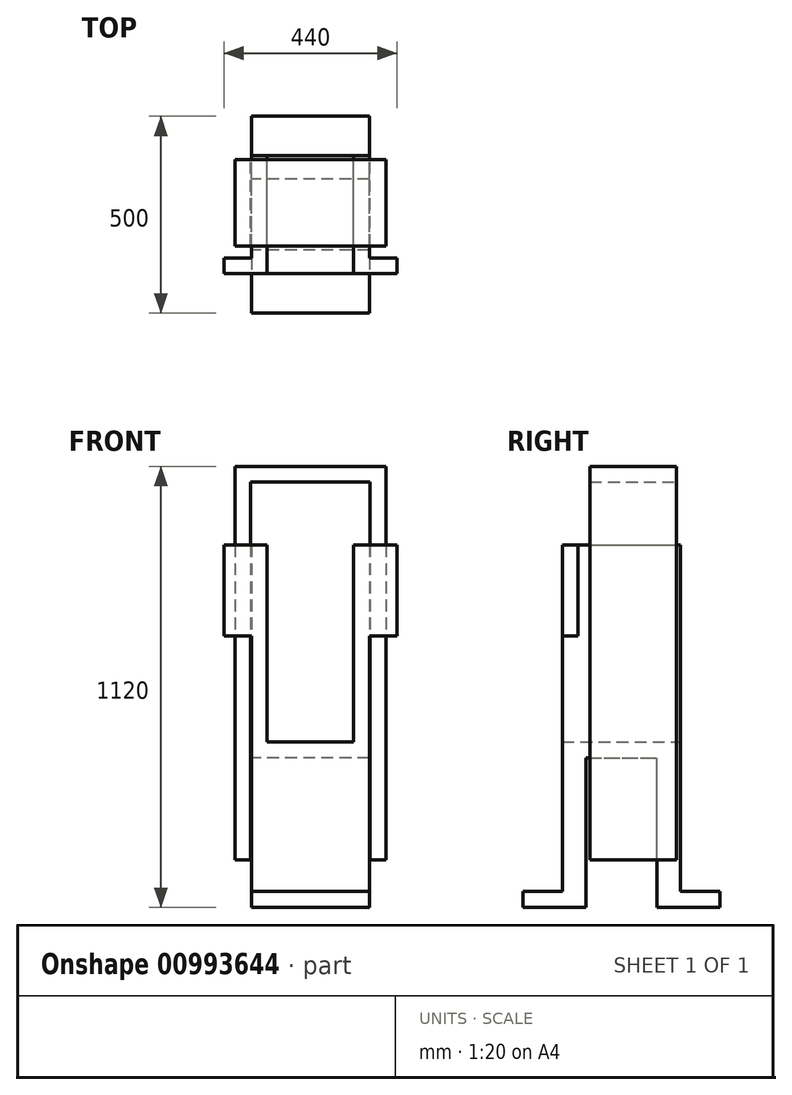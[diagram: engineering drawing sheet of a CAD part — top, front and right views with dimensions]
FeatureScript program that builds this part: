
annotation { "Feature Type Name" : "Feature", "Feature Type Description" : "" }
export const myFeature = defineFeature(function(context is Context, id is Id, definition is map)
    precondition{}
    {
        {
            var Q0;
            Q0=qCreatedBy(makeId("Top.planeOp"),FACE);
            var sketch = newSketch(context, id + "F0", { "sketchPlane" : qUnion([Q0])});
            skLineSegment(sketch, "E0.bottom", {"start": v(150, -150) * mm, "end": v(-150, -150) * mm});
            skLineSegment(sketch, "E0.top", {"start": v(150, 150) * mm, "end": v(-150, 150) * mm});
            skLineSegment(sketch, "E0.left", {"start": v(150, -150) * mm, "end": v(150, 150) * mm});
            skLineSegment(sketch, "E0.right", {"start": v(-150, -150) * mm, "end": v(-150, 150) * mm});
            skPoint(sketch, "E0.middle", {"position": v(0, 0) * mm});
            skSolve(sketch);
        }
        {
            var Q0;
            Q0=makeQuery(id+"F0.imprint","IMPRINT",FACE,{"disambiguationData":[TD([[makeQuery(id+"F0.imprint","IMPRINT",EDGE,{"derivedFrom":sQuery(id+"F0.wireOp",EDGE,"E0.bottom")}),-1.0]])]});
            extrude(context, id + "F1", {"entities" : qUnion([Q0]), "depth" : 40 * mm, "offsetDistance" : 25 * mm});
        }
        {
            var Q0;
            Q0=makeQuery(id+"F1.opExtrude","CAP_FACE",FACE,{"disambiguationData":[OSD([sQuery(id+"F0.wireOp",EDGE,"E0.bottom"),sQuery(id+"F0.wireOp",EDGE,"E0.top"),sQuery(id+"F0.wireOp",EDGE,"E0.left"),sQuery(id+"F0.wireOp",EDGE,"E0.right")])],"isStart":false});
            var sketch = newSketch(context, id + "F2", { "sketchPlane" : qUnion([Q0])});
            skLineSegment(sketch, "E1.bottom", {"start": v(-150, -150) * mm, "end": v(-110, -150) * mm});
            skLineSegment(sketch, "E1.top", {"start": v(-150, 150) * mm, "end": v(-110, 150) * mm});
            skLineSegment(sketch, "E1.left", {"start": v(-150, -150) * mm, "end": v(-150, 150) * mm});
            skLineSegment(sketch, "E1.right", {"start": v(-110, -150) * mm, "end": v(-110, 150) * mm});
            skLineSegment(sketch, "E2.bottom", {"start": v(150, -150) * mm, "end": v(110, -150) * mm});
            skLineSegment(sketch, "E2.top", {"start": v(150, 150) * mm, "end": v(110, 150) * mm});
            skLineSegment(sketch, "E2.left", {"start": v(150, -150) * mm, "end": v(150, 150) * mm});
            skLineSegment(sketch, "E2.right", {"start": v(110, -150) * mm, "end": v(110, 150) * mm});
            skSolve(sketch);
        }
        {
            var Q0;
            Q0=makeQuery(id+"F2.imprint","IMPRINT",FACE,{"disambiguationData":[TD([[makeQuery(id+"F2.imprint","IMPRINT",EDGE,{"derivedFrom":sQuery(id+"F2.wireOp",EDGE,"E1.bottom")}),-1.0]])]});
            var Q1;
            Q1=makeQuery(id+"F2.imprint","IMPRINT",FACE,{"disambiguationData":[TD([[makeQuery(id+"F2.imprint","IMPRINT",EDGE,{"derivedFrom":sQuery(id+"F2.wireOp",EDGE,"E2.bottom")}),-1.0]])]});
            extrude(context, id + "F3", {"entities" : qUnion([Q0, Q1]), "operationType" : NewBodyOperationType.ADD, "depth" : 500 * mm, "offsetDistance" : 25 * mm});
        }
        {
            var Q0;
            Q0=makeQuery(id+"F3.boolean.opBoolean","MERGE",FACE,{"derivedFrom":[makeQuery(id+"F1.opExtrude","SWEPT_FACE",FACE,{"disambiguationData":[OSD([sQuery(id+"F0.wireOp",EDGE,"E0.bottom")])]}),makeQuery(id+"F3.opExtrude","SWEPT_FACE",FACE,{"disambiguationData":[OSD([sQuery(id+"F2.wireOp",EDGE,"E1.bottom")])]}),makeQuery(id+"F3.opExtrude","SWEPT_FACE",FACE,{"disambiguationData":[OSD([sQuery(id+"F2.wireOp",EDGE,"E2.bottom")])]})]});
            var sketch = newSketch(context, id + "F4", { "sketchPlane" : qUnion([Q0])});
            skLineSegment(sketch, "E3.bottom", {"start": v(-150, 540) * mm, "end": v(-220, 540) * mm});
            skLineSegment(sketch, "E3.top", {"start": v(-150, 310) * mm, "end": v(-220, 310) * mm});
            skLineSegment(sketch, "E3.left", {"start": v(-150, 540) * mm, "end": v(-150, 310) * mm});
            skLineSegment(sketch, "E3.right", {"start": v(-220, 540) * mm, "end": v(-220, 310) * mm});
            skLineSegment(sketch, "E4.bottom", {"start": v(150, 540) * mm, "end": v(220, 540) * mm});
            skLineSegment(sketch, "E4.top", {"start": v(150, 310) * mm, "end": v(220, 310) * mm});
            skLineSegment(sketch, "E4.left", {"start": v(150, 540) * mm, "end": v(150, 310) * mm});
            skLineSegment(sketch, "E4.right", {"start": v(220, 540) * mm, "end": v(220, 310) * mm});
            skSolve(sketch);
        }
        {
            var Q0;
            Q0=makeQuery(id+"F4.imprint","IMPRINT",FACE,{"disambiguationData":[TD([[makeQuery(id+"F4.imprint","IMPRINT",EDGE,{"derivedFrom":sQuery(id+"F4.wireOp",EDGE,"E3.bottom")}),1.0]])]});
            var Q1;
            Q1=makeQuery(id+"F4.imprint","IMPRINT",FACE,{"disambiguationData":[TD([[makeQuery(id+"F4.imprint","IMPRINT",EDGE,{"derivedFrom":sQuery(id+"F4.wireOp",EDGE,"E4.bottom")}),-1.0]])]});
            extrude(context, id + "F5", {"entities" : qUnion([Q0, Q1]), "operationType" : NewBodyOperationType.ADD, "oppositeDirection" : true, "depth" : 40 * mm, "offsetDistance" : 25 * mm});
        }
        {
            var Q0;
            Q0=makeQuery(id+"F5.boolean.opBoolean","MERGE",FACE,{"derivedFrom":[makeQuery(id+"F3.opExtrude","CAP_FACE",FACE,{"disambiguationData":[OSD([sQuery(id+"F2.wireOp",EDGE,"E1.bottom"),sQuery(id+"F2.wireOp",EDGE,"E1.top"),sQuery(id+"F2.wireOp",EDGE,"E1.left"),sQuery(id+"F2.wireOp",EDGE,"E1.right")])],"isStart":false}),makeQuery(id+"F5.opExtrude","SWEPT_FACE",FACE,{"disambiguationData":[OSD([sQuery(id+"F4.wireOp",EDGE,"E3.bottom")])]})]});
            var sketch = newSketch(context, id + "F6", { "sketchPlane" : qUnion([Q0])});
            skLineSegment(sketch, "E5.0", {"start": v(-110, 150) * mm, "end": v(-150, 150) * mm, "construction": true});
            skPoint(sketch, "E6.0", {"position": v(220, -110) * mm});
            skPoint(sketch, "E7.0", {"position": v(-220, -110) * mm});
            skPoint(sketch, "E8.0", {"position": v(150, 150) * mm});
            skPoint(sketch, "E9.0", {"position": v(-150, 150) * mm});
            skLineSegment(sketch, "E10.bottom", {"start": v(192, -80) * mm, "end": v(152, -80) * mm});
            skLineSegment(sketch, "E10.top", {"start": v(192, 140) * mm, "end": v(152, 140) * mm});
            skLineSegment(sketch, "E10.left", {"start": v(192, -80) * mm, "end": v(192, 140) * mm});
            skLineSegment(sketch, "E10.right", {"start": v(152, -80) * mm, "end": v(152, 140) * mm});
            skLineSegment(sketch, "E11.MirrorCS", {"start": v(-152, -80) * mm, "end": v(-152, 140) * mm});
            skLineSegment(sketch, "E12.MirrorCS", {"start": v(-192, -80) * mm, "end": v(-192, 140) * mm});
            skLineSegment(sketch, "E13.MirrorCS", {"start": v(-192, 140) * mm, "end": v(-152, 140) * mm});
            skLineSegment(sketch, "E14.MirrorCS", {"start": v(-192, -80) * mm, "end": v(-152, -80) * mm});
            skSolve(sketch);
        }
        {
            var Q0;
            Q0=makeQuery(id+"F6.imprint","IMPRINT",FACE,{"disambiguationData":[TD([[makeQuery(id+"F6.imprint","IMPRINT",EDGE,{"derivedFrom":sQuery(id+"F6.wireOp",EDGE,"E10.bottom")}),-1.0]])]});
            var Q1;
            Q1=makeQuery(id+"F6.imprint","IMPRINT",FACE,{"disambiguationData":[TD([[makeQuery(id+"F6.imprint","IMPRINT",EDGE,{"derivedFrom":sQuery(id+"F6.wireOp",EDGE,"E11.MirrorCS")}),1.0]])]});
            extrude(context, id + "F7", {"entities" : qUnion([Q0, Q1]), "depth" : 200 * mm, "offsetDistance" : 25 * mm});
        }
        {
            var Q0;
            Q0=makeQuery(id+"F7.opExtrude","CAP_FACE",FACE,{"disambiguationData":[OSD([sQuery(id+"F6.wireOp",EDGE,"E10.bottom"),sQuery(id+"F6.wireOp",EDGE,"E10.top"),sQuery(id+"F6.wireOp",EDGE,"E10.left"),sQuery(id+"F6.wireOp",EDGE,"E10.right")])],"isStart":false});
            var sketch = newSketch(context, id + "F8", { "sketchPlane" : qUnion([Q0])});
            skPoint(sketch, "E15.0", {"position": v(-192, 140) * mm});
            skPoint(sketch, "E16.0", {"position": v(192, -80) * mm});
            skLineSegment(sketch, "E17.bottom", {"start": v(192, -80) * mm, "end": v(-192, -80) * mm});
            skLineSegment(sketch, "E17.top", {"start": v(192, 140) * mm, "end": v(-192, 140) * mm});
            skLineSegment(sketch, "E17.left", {"start": v(192, -80) * mm, "end": v(192, 140) * mm});
            skLineSegment(sketch, "E17.right", {"start": v(-192, -80) * mm, "end": v(-192, 140) * mm});
            skSolve(sketch);
        }
        {
            var Q0;
            {var subQ2=sQuery(id+"F8.wireOp",EDGE,"E17.right");Q0=makeQuery(id+"F8.imprint","IMPRINT",FACE,{"disambiguationData":[TD([[makeQuery(id+"F8.imprint","IMPRINT",EDGE,{"derivedFrom":subQ2}),-1.0]])]});}
            extrude(context, id + "F9", {"entities" : qUnion([Q0]), "operationType" : NewBodyOperationType.ADD, "oppositeDirection" : true, "depth" : 40 * mm, "offsetDistance" : 25 * mm});
        }
        {
            var Q0;
            Q0=makeQuery(id+"F7.opExtrude","CAP_FACE",FACE,{"disambiguationData":[OSD([sQuery(id+"F6.wireOp",EDGE,"E10.bottom"),sQuery(id+"F6.wireOp",EDGE,"E10.top"),sQuery(id+"F6.wireOp",EDGE,"E10.left"),sQuery(id+"F6.wireOp",EDGE,"E10.right")])],"isStart":true});
            var Q1;
            Q1=makeQuery(id+"F7.opExtrude","CAP_FACE",FACE,{"disambiguationData":[OSD([sQuery(id+"F6.wireOp",EDGE,"E11.MirrorCS"),sQuery(id+"F6.wireOp",EDGE,"E12.MirrorCS"),sQuery(id+"F6.wireOp",EDGE,"E13.MirrorCS"),sQuery(id+"F6.wireOp",EDGE,"E14.MirrorCS")])],"isStart":true});
            extrude(context, id + "F10", {"entities" : qUnion([Q0, Q1]), "operationType" : NewBodyOperationType.ADD, "depth" : 800 * mm, "offsetDistance" : 25 * mm});
        }
        {
            var Q0;
            Q0=makeQuery(id+"F1.opExtrude","CAP_FACE",FACE,{"disambiguationData":[OSD([sQuery(id+"F0.wireOp",EDGE,"E0.bottom"),sQuery(id+"F0.wireOp",EDGE,"E0.top"),sQuery(id+"F0.wireOp",EDGE,"E0.left"),sQuery(id+"F0.wireOp",EDGE,"E0.right")])],"isStart":true});
            var sketch = newSketch(context, id + "F11", { "sketchPlane" : qUnion([Q0])});
            skPoint(sketch, "E18.0", {"position": v(150, -150) * mm});
            skPoint(sketch, "E19.0", {"position": v(-150, 150) * mm});
            skPoint(sketch, "E20.0", {"position": v(150, 150) * mm});
            skPoint(sketch, "E21.0", {"position": v(-150, -150) * mm});
            skLineSegment(sketch, "E22.bottom", {"start": v(150, -150) * mm, "end": v(-150, -150) * mm});
            skLineSegment(sketch, "E22.top", {"start": v(150, -90) * mm, "end": v(-150, -90) * mm});
            skLineSegment(sketch, "E22.left", {"start": v(150, -150) * mm, "end": v(150, -90) * mm});
            skLineSegment(sketch, "E22.right", {"start": v(-150, -150) * mm, "end": v(-150, -90) * mm});
            skLineSegment(sketch, "E23.MirrorCS", {"start": v(150, 90) * mm, "end": v(-150, 90) * mm});
            skLineSegment(sketch, "E24.MirrorCS", {"start": v(150, 150) * mm, "end": v(150, 90) * mm});
            skLineSegment(sketch, "E25.MirrorCS", {"start": v(150, 150) * mm, "end": v(-150, 150) * mm});
            skLineSegment(sketch, "E26.MirrorCS", {"start": v(-150, 150) * mm, "end": v(-150, 90) * mm});
            skSolve(sketch);
        }
        {
            var Q0;
            Q0=makeQuery(id+"F11.imprint","IMPRINT",FACE,{"disambiguationData":[TD([[makeQuery(id+"F11.imprint","IMPRINT",EDGE,{"derivedFrom":sQuery(id+"F11.wireOp",EDGE,"E22.bottom")}),-1.0]])]});
            var Q1;
            Q1=makeQuery(id+"F11.imprint","IMPRINT",FACE,{"disambiguationData":[TD([[makeQuery(id+"F11.imprint","IMPRINT",EDGE,{"derivedFrom":sQuery(id+"F11.wireOp",EDGE,"E23.MirrorCS")}),-1.0]])]});
            extrude(context, id + "F12", {"entities" : qUnion([Q0, Q1]), "operationType" : NewBodyOperationType.ADD, "depth" : 380 * mm, "offsetDistance" : 25 * mm});
        }
        {
            var Q0;
            Q0=makeQuery(id+"F12.opExtrude","CAP_FACE",FACE,{"disambiguationData":[OSD([sQuery(id+"F11.wireOp",EDGE,"E23.MirrorCS"),sQuery(id+"F11.wireOp",EDGE,"E24.MirrorCS"),sQuery(id+"F11.wireOp",EDGE,"E25.MirrorCS"),sQuery(id+"F11.wireOp",EDGE,"E26.MirrorCS")])],"isStart":false});
            var sketch = newSketch(context, id + "F13", { "sketchPlane" : qUnion([Q0])});
            skPoint(sketch, "E27.middle", {"position": v(0, 0) * mm});
            skLineSegment(sketch, "E28.bottom", {"start": v(-150, 250) * mm, "end": v(150, 250) * mm});
            skLineSegment(sketch, "E28.top", {"start": v(-150, -250) * mm, "end": v(150, -250) * mm});
            skLineSegment(sketch, "E28.left", {"start": v(-150, 250) * mm, "end": v(-150, -250) * mm});
            skLineSegment(sketch, "E28.right", {"start": v(150, 250) * mm, "end": v(150, -250) * mm});
            skLineSegment(sketch, "E29", {"start": v(150, 90) * mm, "end": v(-150, 90) * mm});
            skLineSegment(sketch, "E30.0", {"start": v(150, -90) * mm, "end": v(-150, -90) * mm});
            skSolve(sketch);
        }
        {
            var Q0;
            {var subQ0=sQuery(id+"F13.wireOp",EDGE,"E28.bottom");Q0=makeQuery(id+"F13.imprint","IMPRINT",FACE,{"disambiguationData":[TD([[makeQuery(id+"F13.imprint","IMPRINT",EDGE,{"derivedFrom":subQ0}),-1.0]])]});}
            var Q1;
            {var subQ2=makeQuery(id+"F12.opExtrude","CAP_EDGE",EDGE,{"disambiguationData":[OSD([sQuery(id+"F11.wireOp",EDGE,"E23.MirrorCS")])],"isStart":false});Q1=makeQuery(id+"F13.imprint","IMPRINT",FACE,{"disambiguationData":[TD([[makeQuery(id+"F13.imprint","IMPRINT",EDGE,{"derivedFrom":subQ2}),-1.0]])]});}
            var Q2;
            {var subQ0=sQuery(id+"F13.wireOp",EDGE,"E28.top");Q2=makeQuery(id+"F13.imprint","IMPRINT",FACE,{"disambiguationData":[TD([[makeQuery(id+"F13.imprint","IMPRINT",EDGE,{"derivedFrom":subQ0}),1.0]])]});}
            extrude(context, id + "F14", {"entities" : qUnion([Q0, Q1, Q2]), "operationType" : NewBodyOperationType.ADD, "oppositeDirection" : true, "depth" : 40 * mm, "offsetDistance" : 25 * mm});
        }
    });
